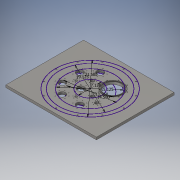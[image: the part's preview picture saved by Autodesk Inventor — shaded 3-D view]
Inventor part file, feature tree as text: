
AUTODESK INVENTOR PART (.ipt)
format: ipt  version: 2018 (Build 220112000, 112)  size: 477,696 bytes
history: native  units: in
note: dims shown in document units (in); Inventor stores cm internally (conversion verified against a paired STEP export)
features: sketch x22, hole x11, extrude x10, pattern_circular x6
ambient origin geometry x8: Origin, YZ Plane, XZ Plane, XY Plane, X Axis, Y Axis, Z Axis, Center Point
bodies: Solid1 (feature_tree)
feature tree (49):
  extrude  "Extrusion1"  Depth=24.0in
  sketch  "Sketch23"  dims[d16=0.252in d17=0.4in d18=0.375in d19=0.25in d20=0.5635in d21=0.5in d22=0.8108in d23=6.5in]
  extrude  "Extrusion2"  Depth=0.75in
  hole  "Hole1"  [1 undecoded]
  extrude  "Extrusion22"  Depth=1.0in TaperAngle=0.0deg
  extrude  "Extrusion29"  Depth=3.1496in TaperAngle=360.0deg
  extrude  "Extrusion3"  Depth=6.5in
  hole  "Hole2"  [1 undecoded]
  pattern_circular  "Circular Pattern1"  Count=8 Angle=360.0deg
  extrude  "Extrusion5"  Depth=3.0in
  extrude  "Extrusion16"  Depth=1.04in
  hole  "Hole9"  [1 undecoded]
  pattern_circular  "Circular Pattern6"  Count=6 Angle=360.0deg
  extrude  "Extrusion18"  Depth=0.0625in
  hole  "Hole10"  [1 undecoded]
  pattern_circular  "Circular Pattern7"  [2 undecoded]
  hole  "Hole13"  [1 undecoded]
  pattern_circular  "Circular Pattern9"  [2 undecoded]
  extrude  "Extrusion23"  Depth=0.0625in TaperAngle=360.0deg
  hole  "Hole19"  [1 undecoded]
  pattern_circular  "Circular Pattern11"  [2 undecoded]
  extrude  "Extrusion27"  Depth=0.0625in TaperAngle=360.0deg
  hole  "Hole23"  [1 undecoded]
  hole  "Hole18"  [1 undecoded]
  pattern_circular  "Circular Pattern12"  [2 undecoded]
  hole  "Hole20"  [1 undecoded]
  hole  "Hole22"  [1 undecoded]
  hole  "Hole24"  [1 undecoded]
  sketch  "Sketch57"  dims[d210=0.7874in d211=90.0deg d221=6.5in d222=0.7902in d223=2.07in d224=0.1in d225=0.0in d229=1.625in d230=3.1496in d232=360.0deg d234=0.156in d235=0.38in d236=0.375in d237=0.25in d238=0.5635in d239=0.536in d240=0.8108in d242=0.7874in d243=90.0deg d277=10.4429in d278=0.354in d279=0.63in d280=0.375in d281=0.25in d282=0.5635in d283=0.831in d284=0.8108in d285=4.7244in d286=360.0deg d288=5.984in d289=6.3in d290=0.125in d291=0.0in d292=7.125in d293=15.125in d294=2.0in d295=135.0deg d296=2.07in d297=0.1in d298=0.0in d321=0.7874in d322=1.3743in d349=5.6in d350=30.0deg d351=1.04in d352=0.1in d353=0.0in d384=6.5in d385=0.0in d388=1.0in d389=45.0deg d390=1.5748in d392=360.0deg d394=0.171in d395=0.432in d396=0.375in d397=0.25in d398=0.5635in d399=0.64in d400=0.8108in d401=1.5748in d402=360.0deg d404=0.5in d405=22.5deg d406=0.5in d407=22.5deg d408=2.0in d409=22.5deg d410=1.625in d411=0.0in d412=3.1496in d414=360.0deg d416=0.156in d417=0.38in d418=0.375in d419=0.25in d420=0.5635in d421=0.536in d422=0.8108in d423=0.9449in d424=0.2268in d425=2.3622in d427=360.0deg d429=0.156in d430=0.38in d431=0.375in d432=0.25in d433=0.5635in d434=0.536in d435=0.8108in d448=0.9449in d449=0.1512in d450=2.3622in d452=360.0deg d454=0.156in d455=0.38in d456=0.375in d457=0.25in d458=0.5635in d459=0.536in d460=0.8108in d461=0.9449in d462=30.0deg d463=2.3622in d465=360.0deg d467=0.156in d468=0.38in d469=0.375in d470=0.25in d471=0.5635in d472=0.536in d473=0.8108in d474=1.625in d475=22.5deg d476=3.1496in d478=360.0deg d480=0.156in d481=0.38in d482=0.375in d483=0.25in d484=0.5635in d485=0.536in d486=0.8108in d487=5.5in d488=5.75in d489=0.0625in d490=0.0in d491=11.25in d492=14.5in]
  sketch  "Sketch1"  dims[d0=28.0in d1=24.0in]
  sketch  "Sketch2"  dims[d2=0.75in d3=0.0in d4=5.0in]
  sketch  "Sketch3"  dims[d5=45.0deg d6=9.35in]
  sketch  "Sketch4"  dims[d7=5.25in d8=1.0in d9=0.0in]
  sketch  "Sketch7"  dims[d10=3.4in d12=3.1496in d14=360.0deg]
  sketch  "Sketch26"  dims[d24=1.4086in d25=2.07in]
  sketch  "Sketch28"  dims[d26=0.1in d27=0.0in]
  sketch  "Sketch30"  dims[d31=1.625in d33=3.1496in d35=360.0deg]
  sketch  "Sketch32"  dims[d37=0.156in d38=0.38in d39=0.375in d40=0.25in d41=0.5635in d42=0.536in d43=0.8108in d44=3.0in]
  sketch  "Sketch37"  dims[d45=0.8589in d46=1.04in]
  sketch  "Sketch38"  dims[d47=0.1in d48=0.0in d134=1.1811in d135=180.0deg]
  sketch  "Sketch39"  dims[d167=21.5in]
  sketch  "Sketch45"  dims[d168=19.125in]
  sketch  "Sketch49"  dims[d185=4.25in]
  sketch  "Sketch50"  dims[d186=180.0deg]
  sketch  "Sketch51"  dims[d187=0.68in]
  sketch  "Sketch53"  dims[d188=0.1in d189=0.0in]
  sketch  "Sketch54"  dims[d193=0.75in]
  sketch  "Sketch55"  dims[d194=180.0deg]
  sketch  "Sketch56"  dims[d195=0.156in d196=0.38in d197=0.375in d198=0.25in d199=0.5635in d200=0.536in d201=0.8108in d202=2.3622in d204=360.0deg]
note: 19 required parameter values undecoded (feature->parameter linkage not recoverable at this tier; creation-order binding heuristic only, values carry confidence <= 0.55)
